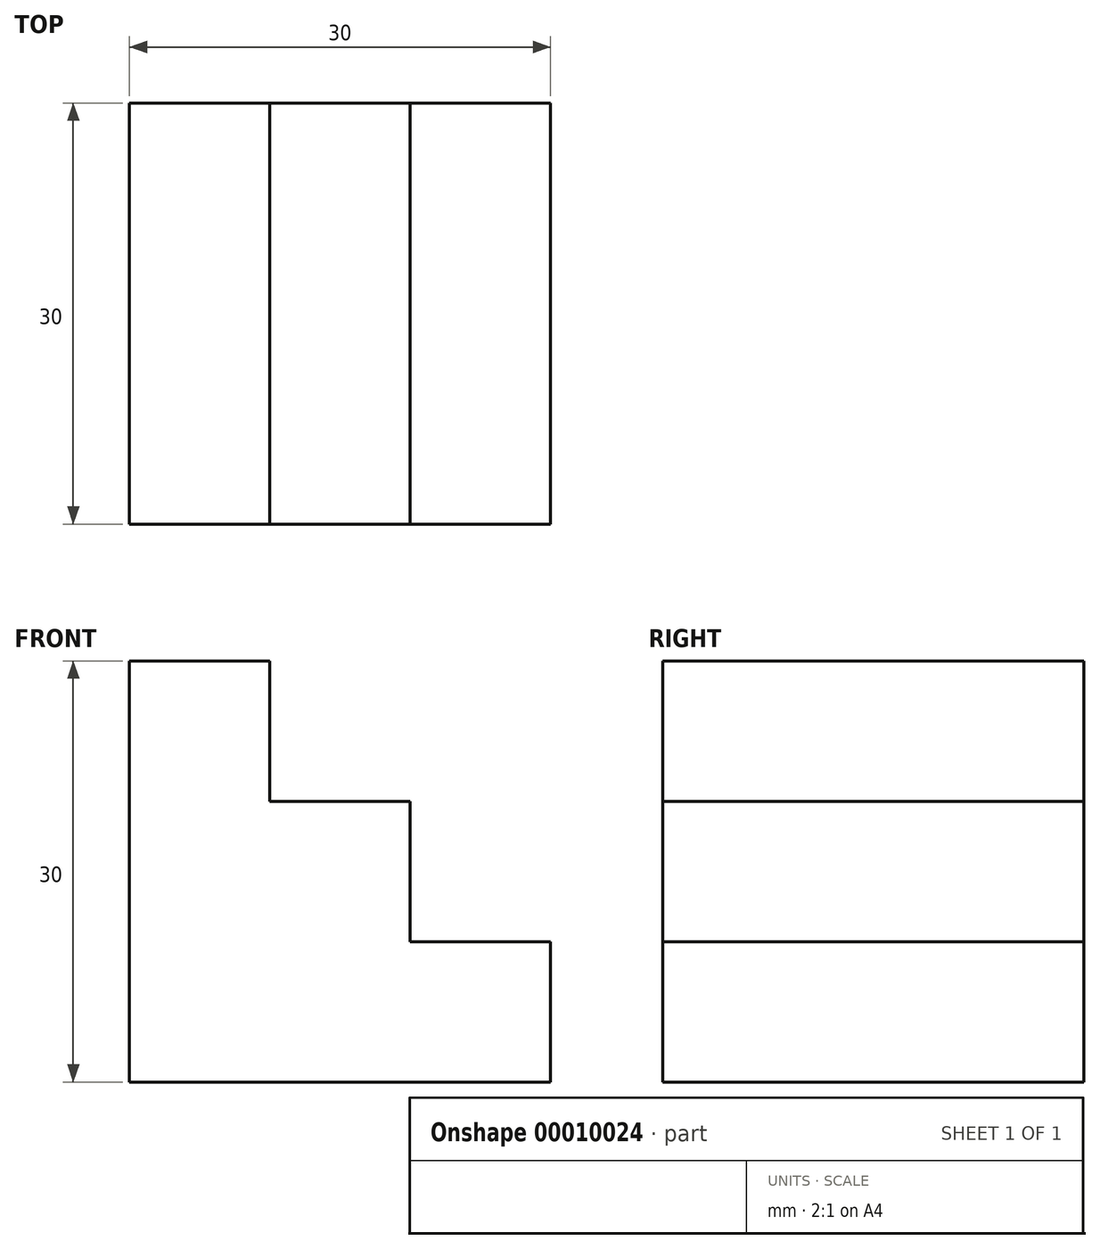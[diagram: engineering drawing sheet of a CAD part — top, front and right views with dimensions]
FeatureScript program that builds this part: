
annotation { "Feature Type Name" : "Feature", "Feature Type Description" : "" }
export const myFeature = defineFeature(function(context is Context, id is Id, definition is map)
    precondition{}
    {
        {
            var Q0;
            Q0=qCreatedBy(makeId("Front.planeOp"),FACE);
            var sketch = newSketch(context, id + "F0", { "sketchPlane" : qUnion([Q0])});
            skLineSegment(sketch, "E0.bottom", {"start": v(0, 0) * mm, "end": v(30, 0) * mm});
            skLineSegment(sketch, "E0.top", {"start": v(0, 30) * mm, "end": v(30, 30) * mm});
            skLineSegment(sketch, "E0.left", {"start": v(0, 0) * mm, "end": v(0, 30) * mm});
            skLineSegment(sketch, "E0.right", {"start": v(30, 0) * mm, "end": v(30, 30) * mm});
            skLineSegment(sketch, "E1.bottom", {"start": v(10, 30) * mm, "end": v(20, 30) * mm});
            skLineSegment(sketch, "E1.top", {"start": v(10, 20) * mm, "end": v(20, 20) * mm});
            skLineSegment(sketch, "E1.left", {"start": v(10, 30) * mm, "end": v(10, 20) * mm});
            skLineSegment(sketch, "E1.right", {"start": v(20, 30) * mm, "end": v(20, 20) * mm});
            skLineSegment(sketch, "E2.bottom", {"start": v(20, 20) * mm, "end": v(30, 20) * mm});
            skLineSegment(sketch, "E2.top", {"start": v(20, 10) * mm, "end": v(30, 10) * mm});
            skLineSegment(sketch, "E2.left", {"start": v(20, 20) * mm, "end": v(20, 10) * mm});
            skLineSegment(sketch, "E2.right", {"start": v(30, 20) * mm, "end": v(30, 10) * mm});
            skSolve(sketch);
        }
        {
            var Q0;
            {var subQ3=sQuery(id+"F0.wireOp",EDGE,"E0.bottom");Q0=makeQuery(id+"F0.imprint","IMPRINT",FACE,{"disambiguationData":[TD([[makeQuery(id+"F0.imprint","IMPRINT",EDGE,{"derivedFrom":subQ3}),1.0]])]});}
            extrude(context, id + "F1", {"entities" : qUnion([Q0]), "depth" : 30 * mm});
        }
    });
